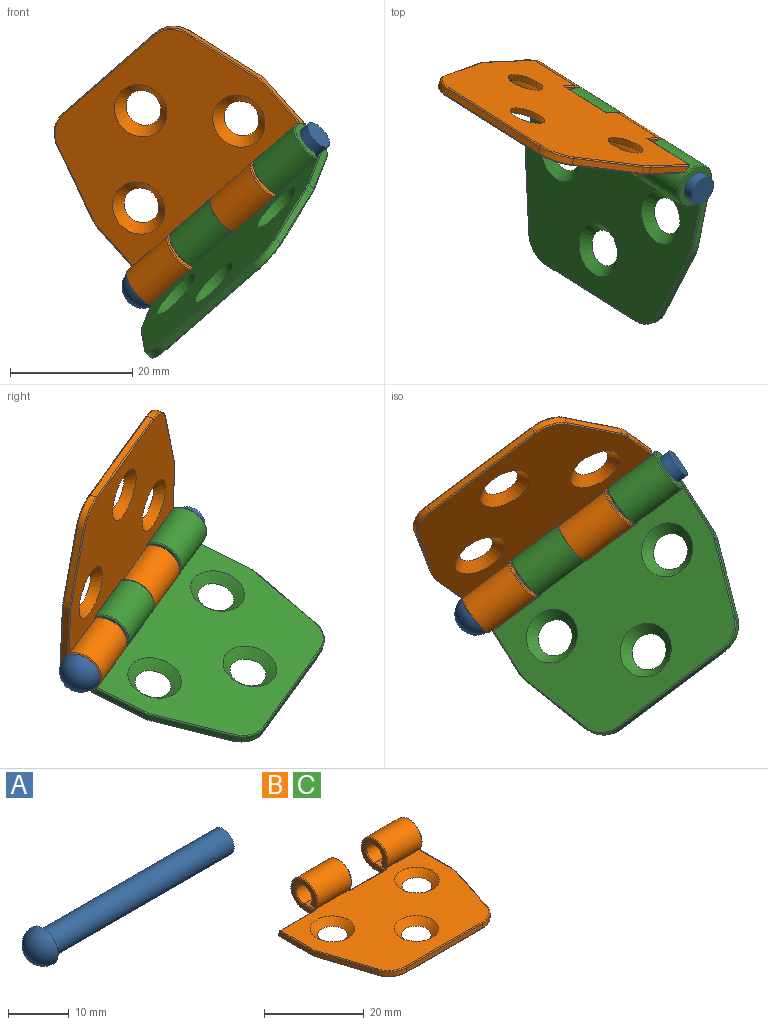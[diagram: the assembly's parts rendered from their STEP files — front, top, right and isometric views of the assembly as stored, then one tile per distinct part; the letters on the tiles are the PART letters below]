
ASSEMBLY  parts=3 mates=2
PART A: 4 faces, bbox 45.5x7x7 mm
  f0: cylinder r=2.48mm len=42mm, axis (-1,0,0), area 653.1mm2, adj f1,f3
  f1: plane 4.95x4.95mm, normal (1,0,0), area 19.2mm2, adj f0
  f2: sphere r=3.5mm, area 77mm2, adj f3
  f3: plane 7x7mm, normal (1,0,0), area 19.2mm2, adj f0,f2
PART B: 64 faces, bbox 40.1x34.5x8.1 mm
  f0: cylinder r=2.25mm len=9.6mm, axis (-1,0,0), area 114mm2, adj f2,f3,f32,f54
  f1: cylinder r=3.75mm len=9.6mm, axis (-1,0,0), area 190.8mm2, adj f2,f4,f36,f59
  f2: plane 10x1.23mm, normal (0,0.58,-0.81), area 15mm2, adj f0,f1,f17,f20,f32,f36,f54,f59
  f3: plane 39.6x29.8mm, normal (0,0,1), area 827.3mm2, adj f0,f7,f13,f14,f15,f26,f27,f28
  f4: plane 39.6x29.8mm, normal (0,0,-1), area 943mm2, adj f1,f8,f13,f14,f15,f39,f41,f44
  f5: plane 21.75x1.1mm, normal (0,-1,0), area 23.9mm2, adj f21,f24,f30,f48
  f6: plane 9.29x1.1mm, normal (-1,0,0), area 9.9mm2, adj f22,f38,f42,f44
  f7: cylinder r=2.25mm len=9.6mm, axis (-1,0,0), area 114mm2, adj f3,f9,f25,f57
  f8: cylinder r=3.75mm len=9.6mm, axis (-1,0,0), area 190.8mm2, adj f4,f9,f53,f62
  f9: plane 10x1.23mm, normal (0,0.58,-0.81), area 15mm2, adj f7,f8,f10,f19,f25,f53,f57,f62
  f10: plane 15.62x7.1mm, normal (1,0,0), area 30.7mm2, adj f9,f23,f25,f26,f52,f53
  f11: plane 12.93x4.13mm, normal (0.95,-0.3,0), area 14.9mm2, adj f23,f24,f28,f50
  f12: plane 12.93x4.13mm, normal (-0.95,-0.3,0), area 14.9mm2, adj f21,f22,f33,f46
  f13: cone r=2.2mm half-angle=45deg, axis (0,0,1), area 49.7mm2, adj f3,f4
  f14: cone r=2.2mm half-angle=45deg, axis (0,0,1), area 49.7mm2, adj f3,f4
  f15: cone r=2.2mm half-angle=45deg, axis (0,0,1), area 49.7mm2, adj f3,f4
  f16: plane 9.82x1.1mm, normal (0,0.91,0.41), area 11.8mm2, adj f17,f34,f37,f41,f42
  f17: plane 7.1x7.1mm, normal (-1,0,0), area 20.6mm2, adj f2,f16,f32,f34,f36,f39,f41
  f18: plane 10.04x1.1mm, normal (0,0.91,0.41), area 12.1mm2, adj f19,f20,f55,f56,f58,f61
  f19: plane 7.1x7.1mm, normal (-1,0,0), area 20.6mm2, adj f9,f18,f57,f58,f61,f62,f63
  f20: plane 7.1x7.1mm, normal (1,0,0), area 20.6mm2, adj f2,f18,f54,f55,f59,f60,f61
  f21: cylinder r=5mm len=4.76mm, axis (0,0,-1), area 6.9mm2, adj f5,f12,f31,f47
  f22: cylinder r=5mm len=1.52mm, axis (0,0,1), area 1.7mm2, adj f6,f12,f35,f45
  f23: cylinder r=5mm len=1.52mm, axis (0,0,-1), area 1.7mm2, adj f10,f11,f27,f51
  f24: cylinder r=5mm len=4.76mm, axis (0,0,1), area 6.9mm2, adj f5,f11,f29,f49
  f25: torus R=2.45mm, axis (1,0,0), area 3.9mm2, adj f7,f9,f10,f26
  f26: cylinder r=0.2mm len=12.07mm, axis (0,1,0), area 3.8mm2, adj f3,f10,f25,f27
  f27: torus R=4.8mm, axis (0,0,1), area 0.5mm2, adj f3,f23,f26,f28
  f28: cylinder r=0.2mm len=12.99mm, axis (0.3,0.95,0), area 4.3mm2, adj f3,f11,f27,f29
  f29: torus R=4.8mm, axis (0,0,1), area 2mm2, adj f3,f24,f28,f30
  f30: cylinder r=0.2mm len=21.75mm, axis (-1,0,0), area 6.8mm2, adj f3,f5,f29,f31
  f31: torus R=4.8mm, axis (0,0,1), area 2mm2, adj f3,f21,f30,f33
  f32: torus R=2.45mm, axis (1,0,0), area 3.9mm2, adj f0,f2,f17,f34
  f33: cylinder r=0.2mm len=12.99mm, axis (0.3,-0.95,0), area 4.3mm2, adj f3,f12,f31,f35
  f34: cylinder r=0.2mm len=3.28mm, axis (0,-1,0), area 1mm2, adj f3,f16,f17,f32,f37
  f35: torus R=4.8mm, axis (0,0,1), area 0.5mm2, adj f3,f22,f33,f38
  f36: torus R=3.55mm, axis (1,0,0), area 6.1mm2, adj f1,f2,f17,f39
  f37: cylinder r=0.2mm len=10mm, axis (-1,0,0), area 2.3mm2, adj f3,f16,f34,f40
  f38: cylinder r=0.2mm len=8.79mm, axis (0,-1,0), area 2.8mm2, adj f3,f6,f35,f40
  f39: cylinder r=0.2mm len=2.78mm, axis (0,1,0), area 0.8mm2, adj f4,f17,f36,f41
  f40: sphere r=0.2mm, area 0mm2, adj f37,f38,f42
  f41: cylinder r=0.2mm len=10mm, axis (1,0,0), area 3.9mm2, adj f4,f16,f17,f39,f43
  f42: cylinder r=0.2mm len=1.18mm, axis (0,-0.41,0.91), area 0.4mm2, adj f6,f16,f40,f43
  f43: sphere r=0.2mm, area 0.1mm2, adj f41,f42,f44
  f44: cylinder r=0.2mm len=9.29mm, axis (0,1,0), area 2.9mm2, adj f4,f6,f43,f45
  f45: torus R=4.8mm, axis (0,0,1), area 0.5mm2, adj f4,f22,f44,f46
  f46: cylinder r=0.2mm len=12.99mm, axis (-0.3,0.95,0), area 4.3mm2, adj f4,f12,f45,f47
  f47: torus R=4.8mm, axis (0,0,1), area 2mm2, adj f4,f21,f46,f48
  f48: cylinder r=0.2mm len=21.75mm, axis (1,0,0), area 6.8mm2, adj f4,f5,f47,f49
  f49: torus R=4.8mm, axis (0,0,1), area 2mm2, adj f4,f24,f48,f50
  f50: cylinder r=0.2mm len=12.99mm, axis (-0.3,-0.95,0), area 4.3mm2, adj f4,f11,f49,f51
  f51: torus R=4.8mm, axis (0,0,1), area 0.5mm2, adj f4,f23,f50,f52
  f52: cylinder r=0.2mm len=12.07mm, axis (0,-1,0), area 3.8mm2, adj f4,f10,f51,f53
  f53: torus R=3.55mm, axis (1,0,0), area 6.1mm2, adj f8,f9,f10,f52
  f54: torus R=2.45mm, axis (1,0,0), area 3.9mm2, adj f0,f2,f20,f55
  f55: cylinder r=0.2mm len=3.28mm, axis (0,1,0), area 1mm2, adj f3,f18,f20,f54,f56
  f56: cylinder r=0.2mm len=10.4mm, axis (-1,0,0), area 2.3mm2, adj f3,f18,f55,f58
  f57: torus R=2.45mm, axis (1,0,0), area 3.9mm2, adj f7,f9,f19,f58
  f58: cylinder r=0.2mm len=3.28mm, axis (0,-1,0), area 1mm2, adj f3,f18,f19,f56,f57
  f59: torus R=3.55mm, axis (1,0,0), area 6.1mm2, adj f1,f2,f20,f60
  f60: cylinder r=0.2mm len=2.78mm, axis (0,-1,0), area 0.8mm2, adj f4,f20,f59,f61
  f61: cylinder r=0.2mm len=10.4mm, axis (1,0,0), area 4mm2, adj f4,f18,f19,f20,f60,f63
  f62: torus R=3.55mm, axis (1,0,0), area 6.1mm2, adj f8,f9,f19,f63
  f63: cylinder r=0.2mm len=2.78mm, axis (0,1,0), area 0.8mm2, adj f4,f19,f61,f62
PART C: same geometry as B
PLACE A rot(axis=(-0.92,0.2,-0.35),169.5deg) t=(-33.63,59.5,-43.28)mm
PLACE B rot(axis=(0.39,0.71,-0.58),168.3deg) t=(-13.89,45.46,-8.98)mm
PLACE C rot(axis=(0.41,-0.83,-0.38),51.7deg) t=(-33.04,48.84,-51.34)mm
MATE fastened A.f0 <-> B.f0  axis (-0.68,0.43,-0.59) through (-33.63,59.5,-43.28)mm
MATE revolute B.f0 <-> C.f0  axis (0.68,-0.43,0.59) through (-19.99,50.93,-31.44)mm
